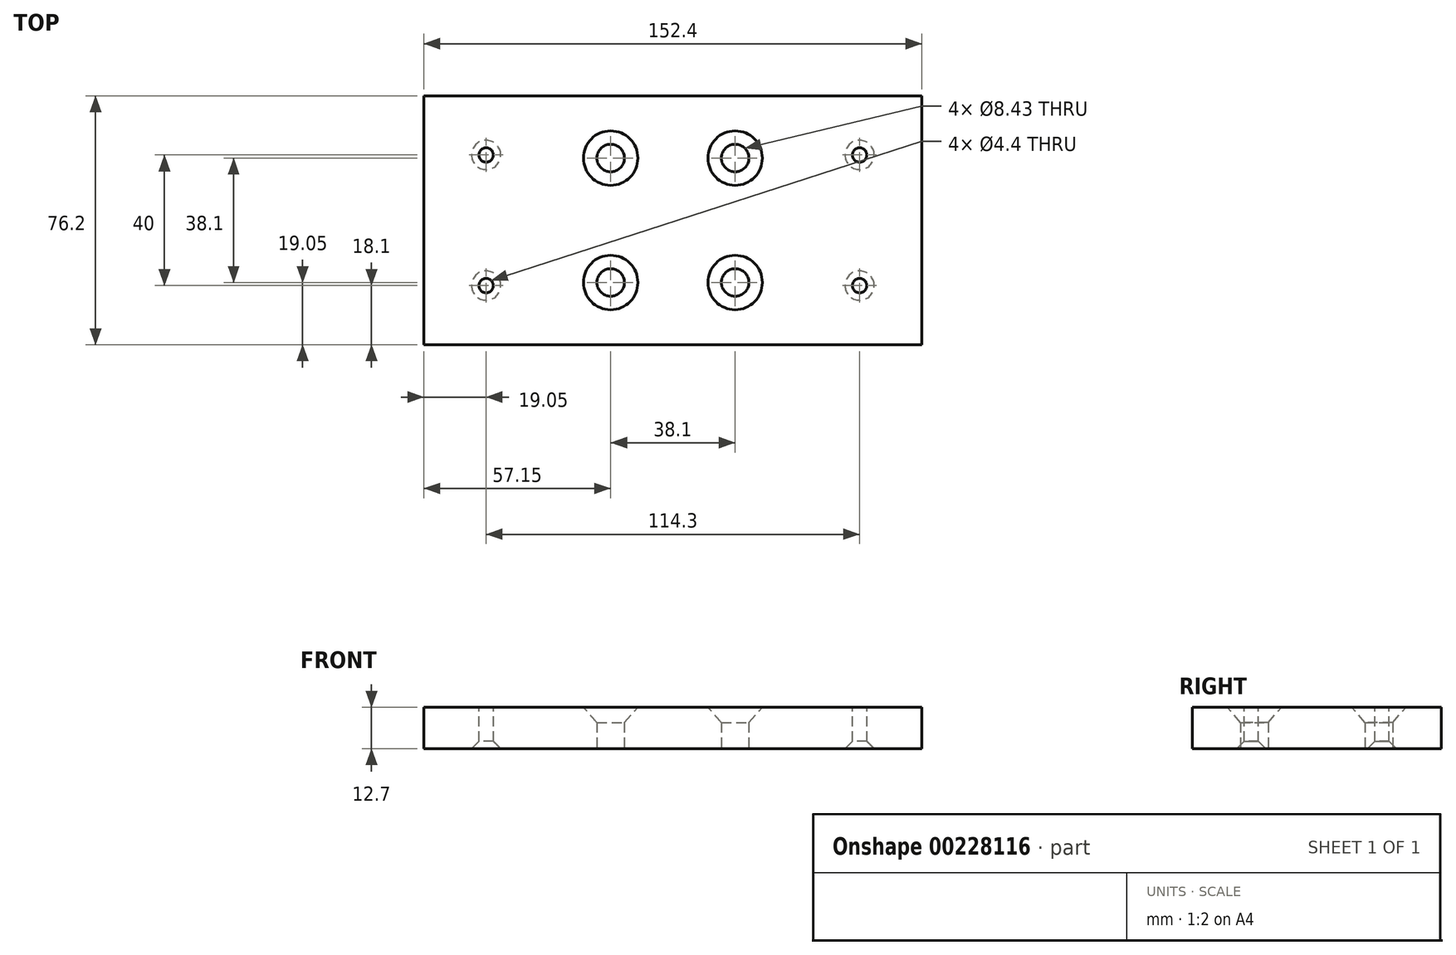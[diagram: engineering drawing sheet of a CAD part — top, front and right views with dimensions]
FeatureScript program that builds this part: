
annotation { "Feature Type Name" : "Feature", "Feature Type Description" : "" }
export const myFeature = defineFeature(function(context is Context, id is Id, definition is map)
    precondition{}
    {
        {
            var Q0;
            Q0=qCreatedBy(makeId("Top.planeOp"),FACE);
            var sketch = newSketch(context, id + "F0", { "sketchPlane" : qUnion([Q0])});
            skLineSegment(sketch, "E0.bottom", {"start": v(76.2, -38.1) * mm, "end": v(-76.2, -38.1) * mm});
            skLineSegment(sketch, "E0.top", {"start": v(76.2, 38.1) * mm, "end": v(-76.2, 38.1) * mm});
            skLineSegment(sketch, "E0.left", {"start": v(76.2, -38.1) * mm, "end": v(76.2, 38.1) * mm});
            skLineSegment(sketch, "E0.right", {"start": v(-76.2, -38.1) * mm, "end": v(-76.2, 38.1) * mm});
            skPoint(sketch, "E0.middle", {"position": v(0, 0) * mm});
            skSolve(sketch);
        }
        {
            var Q0;
            Q0=qSketchRegion(id+"F0",true);
            extrude(context, id + "F1", {"entities" : qUnion([Q0]), "depth" : 12.7 * mm, "symmetric" : true});
        }
        {
            var Q0;
            Q0=makeQuery(id+"F1.opExtrude","CAP_FACE",FACE,{"disambiguationData":[OSD([sQuery(id+"F0.wireOp",EDGE,"E0.bottom"),sQuery(id+"F0.wireOp",EDGE,"E0.top"),sQuery(id+"F0.wireOp",EDGE,"E0.left"),sQuery(id+"F0.wireOp",EDGE,"E0.right")])],"isStart":false});
            var sketch = newSketch(context, id + "F2", { "sketchPlane" : qUnion([Q0])});
            skPoint(sketch, "E1", {"position": v(-19.05, 19.05) * mm});
            skPoint(sketch, "E2", {"position": v(19.05, 19.05) * mm});
            skPoint(sketch, "E3", {"position": v(19.05, -19.05) * mm});
            skPoint(sketch, "E4", {"position": v(-19.05, -19.05) * mm});
            skSolve(sketch);
        }
        {
            var Q0;
            Q0=sQuery(id+"F2.wireOp",VERTEX,"E1");
            var Q1;
            Q1=sQuery(id+"F2.wireOp",VERTEX,"E2");
            var Q2;
            Q2=sQuery(id+"F2.wireOp",VERTEX,"E3");
            var Q3;
            Q3=sQuery(id+"F2.wireOp",VERTEX,"E4");
            var Q4;
            Q4=makeQuery(id+"F1.opExtrude","SWEPT_BODY",BODY,{"disambiguationData":[OSD([sQuery(id+"F0.wireOp",EDGE,"E0.bottom"),sQuery(id+"F0.wireOp",EDGE,"E0.top"),sQuery(id+"F0.wireOp",EDGE,"E0.left"),sQuery(id+"F0.wireOp",EDGE,"E0.right")])]});
            hole(context, id + "F3", {"style" : HoleStyle.C_SINK, "endStyle" : HoleEndStyle.THROUGH, "standardTappedOrClearance" : lookupTablePath({ "standard" : "ANSI", "fit" : "Normal (ASME)", "size" : "5/16", "type" : "Clearance" }), "standardBlindInLast" : lookupTablePath({ "fit" : "Free", "standard" : "ANSI", "size" : "5/16", "type" : "Clearance" }), "holeDiameter" : 8.43 * mm, "cSinkDiameter" : 16.66 * mm, "cSinkAngle" : 82 * degree, "locations" : qUnion([Q0, Q1, Q2, Q3]), "scope" : qUnion([Q4]), "isTappedThrough" : true, "startStyle" : HoleStartStyle.SKETCH});
        }
        {
            var Q0;
            Q0=makeQuery(id+"F1.opExtrude","CAP_FACE",FACE,{"disambiguationData":[OSD([sQuery(id+"F0.wireOp",EDGE,"E0.bottom"),sQuery(id+"F0.wireOp",EDGE,"E0.top"),sQuery(id+"F0.wireOp",EDGE,"E0.left"),sQuery(id+"F0.wireOp",EDGE,"E0.right")])],"isStart":true});
            var sketch = newSketch(context, id + "F4", { "sketchPlane" : qUnion([Q0])});
            skPoint(sketch, "E5", {"position": v(-57.15, 20) * mm});
            skPoint(sketch, "E6", {"position": v(57.15, 20) * mm});
            skPoint(sketch, "E7", {"position": v(57.15, -20) * mm});
            skPoint(sketch, "E8", {"position": v(-57.15, -20) * mm});
            skCircle(sketch, "E9", {"center": v(57.15, -20) * mm, "radius": 2.25 * mm});
            skCircle(sketch, "E10.MirrorC", {"center": v(-57.15, -20) * mm, "radius": 2.25 * mm});
            skCircle(sketch, "E11.MirrorC", {"center": v(-57.15, 20) * mm, "radius": 2.25 * mm});
            skCircle(sketch, "E12.MirrorC", {"center": v(57.15, 20) * mm, "radius": 2.25 * mm});
            skSolve(sketch);
        }
        {
            var Q0;
            Q0=sQuery(id+"F4.wireOp",VERTEX,"E5");
            var Q1;
            Q1=sQuery(id+"F4.wireOp",VERTEX,"E6");
            var Q2;
            Q2=sQuery(id+"F4.wireOp",VERTEX,"E7");
            var Q3;
            Q3=sQuery(id+"F4.wireOp",VERTEX,"E8");
            var Q4;
            Q4=makeQuery(id+"F1.opExtrude","SWEPT_BODY",BODY,{"disambiguationData":[OSD([sQuery(id+"F0.wireOp",EDGE,"E0.bottom"),sQuery(id+"F0.wireOp",EDGE,"E0.top"),sQuery(id+"F0.wireOp",EDGE,"E0.left"),sQuery(id+"F0.wireOp",EDGE,"E0.right")])]});
            hole(context, id + "F5", {"style" : HoleStyle.C_SINK, "endStyle" : HoleEndStyle.THROUGH, "standardTappedOrClearance" : lookupTablePath({ "standard" : "ISO", "fit" : "Normal", "size" : "M4", "type" : "Clearance" }), "standardBlindInLast" : lookupTablePath({ "fit" : "Standard", "standard" : "ISO", "size" : "M4", "type" : "Clearance" }), "holeDiameter" : 4.4 * mm, "cSinkDiameter" : 8.96 * mm, "cSinkAngle" : 90 * degree, "locations" : qUnion([Q0, Q1, Q2, Q3]), "scope" : qUnion([Q4]), "tappedDepth" : 12.7 * mm, "tapClearance" : 3, "startStyle" : HoleStartStyle.SKETCH});
        }
    });
